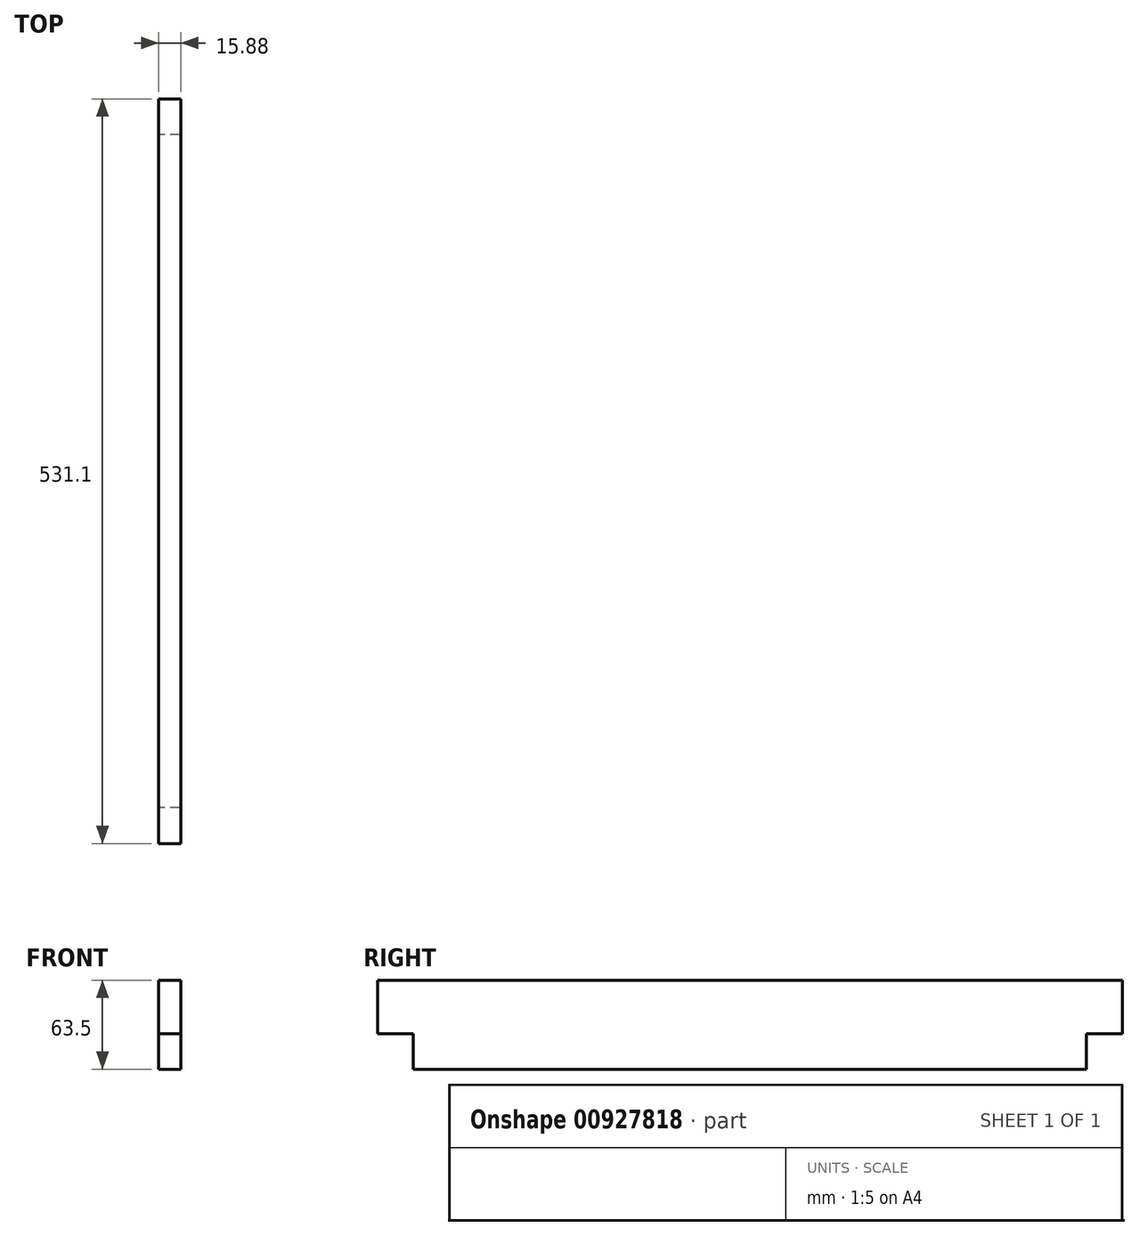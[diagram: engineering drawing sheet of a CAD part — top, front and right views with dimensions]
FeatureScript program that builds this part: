
annotation { "Feature Type Name" : "Feature", "Feature Type Description" : "" }
export const myFeature = defineFeature(function(context is Context, id is Id, definition is map)
    precondition{}
    {
        {
            var Q0;
            Q0=qCreatedBy(makeId("Right.planeOp"),FACE);
            var sketch = newSketch(context, id + "F0", { "sketchPlane" : qUnion([Q0])});
            skLineSegment(sketch, "E0", {"start": v(0, 0) * mm, "end": v(0, 25.4) * mm});
            skLineSegment(sketch, "E1", {"start": v(0, 25.4) * mm, "end": v(-25.55, 25.4) * mm});
            skLineSegment(sketch, "E2", {"start": v(-25.55, 25.4) * mm, "end": v(-25.55, 63.5) * mm});
            skLineSegment(sketch, "E3", {"start": v(-25.55, 63.5) * mm, "end": v(505.55, 63.5) * mm});
            skLineSegment(sketch, "E4", {"start": v(505.55, 63.5) * mm, "end": v(505.55, 25.4) * mm});
            skLineSegment(sketch, "E5", {"start": v(505.55, 25.4) * mm, "end": v(480, 25.4) * mm});
            skLineSegment(sketch, "E6", {"start": v(480, 25.4) * mm, "end": v(480, 0) * mm});
            skLineSegment(sketch, "E7", {"start": v(480, 0) * mm, "end": v(0, 0) * mm});
            skSolve(sketch);
        }
        {
            var Q0;
            Q0=qSketchRegion(id+"F0",true);
            extrude(context, id + "F1", {"entities" : qUnion([Q0]), "depth" : 15.88 * mm, "offsetDistance" : 25 * mm});
        }
    });
